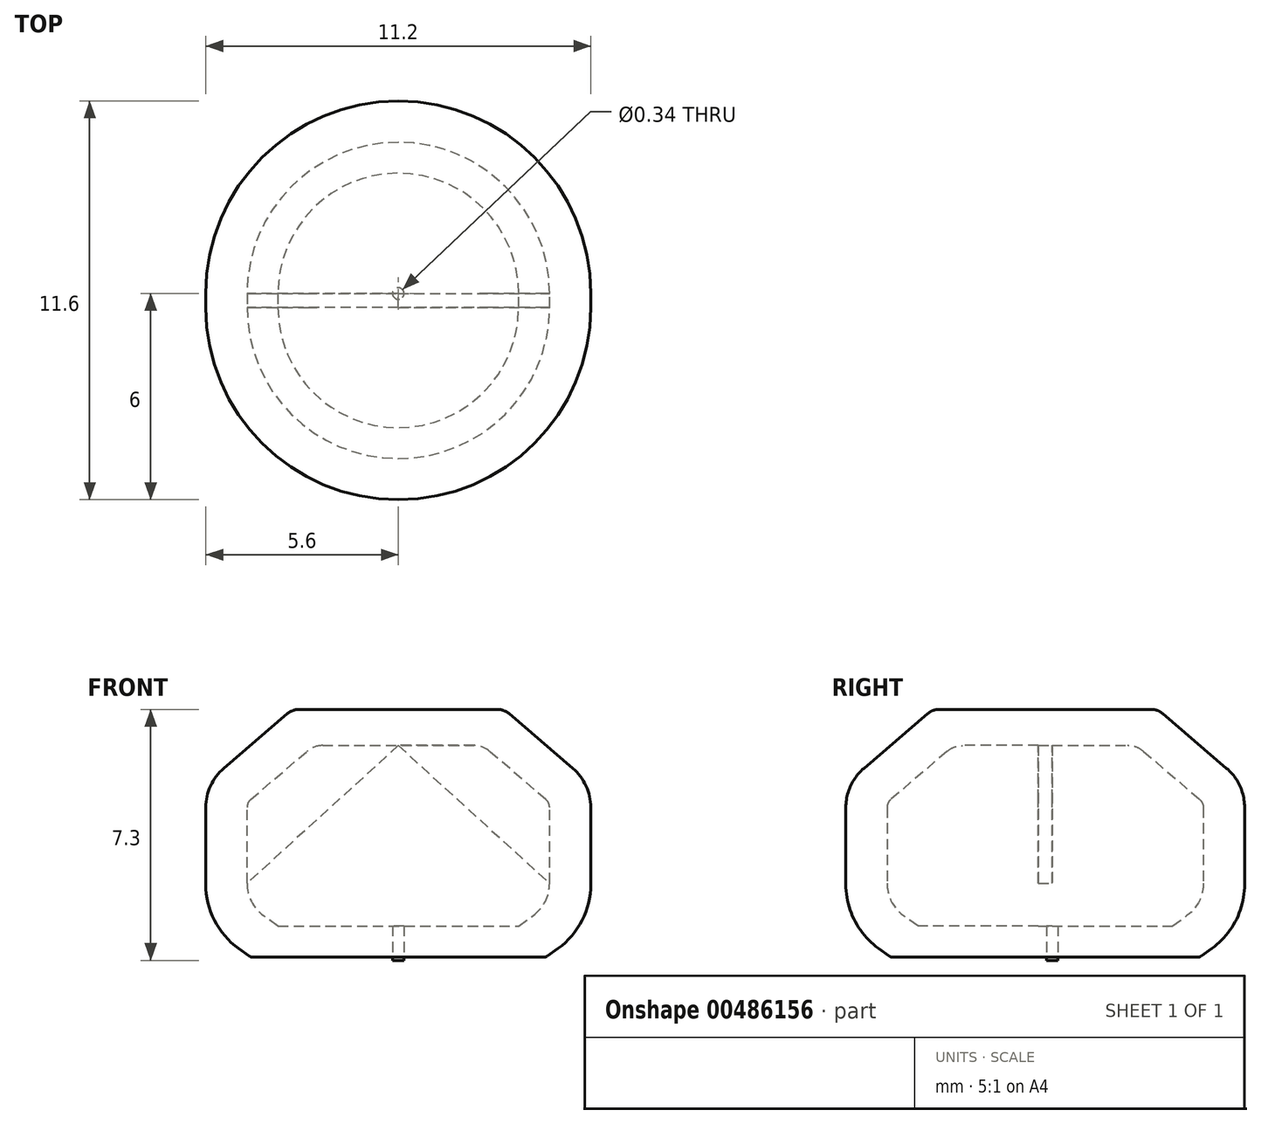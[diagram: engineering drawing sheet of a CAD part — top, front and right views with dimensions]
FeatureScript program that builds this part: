
annotation { "Feature Type Name" : "Feature", "Feature Type Description" : "" }
export const myFeature = defineFeature(function(context is Context, id is Id, definition is map)
    precondition{}
    {
        {
            assignVariable(context, id + "F0", {"name" : "l2", "anyValue" : 0.4});
        }
        {
            var Q0;
            Q0=qCreatedBy(makeId("Front.planeOp"),FACE);
            var sketch = newSketch(context, id + "F1", { "sketchPlane" : qUnion([Q0])});
            skLineSegment(sketch, "E0", {"start": v(0, 0) * mm, "end": v(4.27, 0) * mm});
            skLineSegment(sketch, "E1", {"start": v(5.6, 2.11) * mm, "end": v(5.6, 4.35) * mm});
            skLineSegment(sketch, "E2", {"start": v(2.9, 7.2) * mm, "end": v(0, 7.2) * mm});
            skLineSegment(sketch, "E3", {"start": v(4.33, 0.02) * mm, "end": v(4.65, 0.25) * mm});
            skLineSegment(sketch, "E4", {"start": v(5.08, 5.49) * mm, "end": v(3.22, 7.08) * mm});
            skLineSegment(sketch, "E5", {"start": v(0, 0) * mm, "end": v(0, 0.9) * mm});
            skLineSegment(sketch, "E6", {"start": v(0, 0.9) * mm, "end": v(3.5, 0.9) * mm});
            skLineSegment(sketch, "E7", {"start": v(4.4, 2.14) * mm, "end": v(4.4, 4.35) * mm});
            skLineSegment(sketch, "E8", {"start": v(4.3, 4.58) * mm, "end": v(2.66, 5.98) * mm});
            skLineSegment(sketch, "E9", {"start": v(2.2, 6.15) * mm, "end": v(0, 6.15) * mm});
            skLineSegment(sketch, "E10", {"start": v(0, 6.15) * mm, "end": v(0, 7.2) * mm});
            skLineSegment(sketch, "E11", {"start": v(3.5, 0.9) * mm, "end": v(3.92, 1.2) * mm});
            skPoint(sketch, "E12.visualSharp", {"position": v(5.6, 0.94) * mm});
            skArc(sketch, "E12.filletArc", {"start": v(4.65, 0.25) * mm, "mid": v(5.35, 1.06) * mm, "end": v(5.6, 2.11) * mm});
            skPoint(sketch, "E13.visualSharp", {"position": v(5.6, 5.04) * mm});
            skArc(sketch, "E13.filletArc", {"start": v(5.6, 4.35) * mm, "mid": v(5.46, 4.98) * mm, "end": v(5.08, 5.49) * mm});
            skPoint(sketch, "E14.visualSharp", {"position": v(3.08, 7.2) * mm});
            skArc(sketch, "E14.filletArc", {"start": v(3.22, 7.08) * mm, "mid": v(3.07, 7.17) * mm, "end": v(2.9, 7.2) * mm});
            skPoint(sketch, "E15.visualSharp", {"position": v(2.46, 6.15) * mm});
            skArc(sketch, "E15.filletArc", {"start": v(2.66, 5.98) * mm, "mid": v(2.45, 6.1) * mm, "end": v(2.2, 6.15) * mm});
            skPoint(sketch, "E16.visualSharp", {"position": v(4.4, 4.49) * mm});
            skArc(sketch, "E16.filletArc", {"start": v(4.4, 4.35) * mm, "mid": v(4.37, 4.48) * mm, "end": v(4.3, 4.58) * mm});
            skPoint(sketch, "E17.visualSharp", {"position": v(4.4, 1.55) * mm});
            skArc(sketch, "E17.filletArc", {"start": v(3.92, 1.2) * mm, "mid": v(4.27, 1.61) * mm, "end": v(4.4, 2.14) * mm});
            skPoint(sketch, "E18.visualSharp", {"position": v(4.3, 0) * mm});
            skArc(sketch, "E18.filletArc", {"start": v(4.27, 0) * mm, "mid": v(4.3, 0) * mm, "end": v(4.33, 0.02) * mm});
            skSolve(sketch);
        }
        {
            var Q0;
            Q0=makeQuery(id+"F1.imprint","IMPRINT",FACE,{"disambiguationData":[TD([[makeQuery(id+"F1.imprint","IMPRINT",EDGE,{"derivedFrom":sQuery(id+"F1.wireOp",EDGE,"E0")}),1.0]])]});
            extrude(context, id + "F2", {"entities" : qUnion([Q0]), "depth" : (getVariable(context, 'l2')) * mm, "offsetDistance" : 25 * mm});
        }
        {
            var Q1;
            Q1=makeQuery(id+"F2.opExtrude","SWEPT_FACE",FACE,{"disambiguationData":[OSD([sQuery(id+"F1.wireOp",EDGE,"E9")])]});
            var Q2;
            Q2=makeQuery(id+"F2.opExtrude","SWEPT_FACE",FACE,{"disambiguationData":[OSD([sQuery(id+"F1.wireOp",EDGE,"E7")])]});
            loft(context, id + "F3", {"operationType" : NewBodyOperationType.ADD, "sheetProfilesArray" : [{ "sheetProfileEntities" : qUnion([Q1]) }, { "sheetProfileEntities" : qUnion([Q2]) }]});
        }
        {
            var Q1;
            Q1=makeQuery(id+"F2.opExtrude","SWEPT_FACE",FACE,{"disambiguationData":[OSD([sQuery(id+"F1.wireOp",EDGE,"E15.filletArc")])]});
            var Q2;
            Q2=makeQuery(id+"F2.opExtrude","SWEPT_FACE",FACE,{"disambiguationData":[OSD([sQuery(id+"F1.wireOp",EDGE,"E16.filletArc")])]});
            loft(context, id + "F4", {"operationType" : NewBodyOperationType.ADD, "sheetProfilesArray" : [{ "sheetProfileEntities" : qUnion([Q1]) }, { "sheetProfileEntities" : qUnion([Q2]) }]});
        }
        {
            var Q0;
            Q0=makeQuery(id+"F1.imprint","IMPRINT",FACE,{"disambiguationData":[TD([[makeQuery(id+"F1.imprint","IMPRINT",EDGE,{"derivedFrom":sQuery(id+"F1.wireOp",EDGE,"E0")}),1.0]])]});
            var Q1;
            Q1=sQuery(id+"F1.wireOp",EDGE,"E10");
            revolve(context, id + "F5", {"operationType" : NewBodyOperationType.ADD, "entities" : qUnion([Q0]), "axis" : qUnion([Q1]), "revolveType" : RevolveType.ONE_DIRECTION, "angle" : 180 * degree, "surfaceOperationType" : NewSurfaceOperationType.NEW});
        }
        {
            var Q0;
            Q0=qCreatedBy(makeId("Front.planeOp"),FACE);
            var sketch = newSketch(context, id + "F6", { "sketchPlane" : qUnion([Q0])});
            skLineSegment(sketch, "E19", {"start": v(0, 0) * mm, "end": v(-0.4, 0) * mm});
            skLineSegment(sketch, "E20", {"start": v(-0.4, 0) * mm, "end": v(-0.4, 0.13) * mm});
            skSolve(sketch);
        }
        {
            var Q0;
            Q0=qCreatedBy(makeId("Front.planeOp"),FACE);
            cPlane(context, id + "F7", {"entities" : qUnion([Q0]), "cplaneType" : CPlaneType.OFFSET, "offset" : (getVariable(context, 'l2') / 2) * mm, "width" : 150 * mm, "height" : 150 * mm});
        }
        {
            var Q0;
            Q0=qCreatedBy(id+"F7.planeOp",FACE);
            var sketch = newSketch(context, id + "F8", { "sketchPlane" : qUnion([Q0])});
            skLineSegment(sketch, "E21", {"start": v(0, 0.03) * mm, "end": v(-0.2, 0.03) * mm});
            skLineSegment(sketch, "E22", {"start": v(-0.2, 0.03) * mm, "end": v(-0.2, 0.22) * mm});
            skLineSegment(sketch, "E23", {"start": v(0, 0.03) * mm, "end": v(0, 0.08) * mm});
            skLineSegment(sketch, "E24", {"start": v(0, 0.03) * mm, "end": v(0, 0.14) * mm});
            skPoint(sketch, "E24.endSnap0", {"position": v(0, 0.05) * mm});
            skSolve(sketch);
        }
        {
            var Q0;
            Q0=makeQuery(id+"F2.opExtrude","SWEPT_BODY",BODY,{"disambiguationData":[OSD([sQuery(id+"F1.wireOp",EDGE,"E0"),sQuery(id+"F1.wireOp",EDGE,"E1"),sQuery(id+"F1.wireOp",EDGE,"E2"),sQuery(id+"F1.wireOp",EDGE,"E3"),sQuery(id+"F1.wireOp",EDGE,"E4"),sQuery(id+"F1.wireOp",EDGE,"E5"),sQuery(id+"F1.wireOp",EDGE,"E6"),sQuery(id+"F1.wireOp",EDGE,"E7"),sQuery(id+"F1.wireOp",EDGE,"E8"),sQuery(id+"F1.wireOp",EDGE,"E9"),sQuery(id+"F1.wireOp",EDGE,"E10"),sQuery(id+"F1.wireOp",EDGE,"E11"),sQuery(id+"F1.wireOp",EDGE,"E12.filletArc"),sQuery(id+"F1.wireOp",EDGE,"E13.filletArc"),sQuery(id+"F1.wireOp",EDGE,"E14.filletArc"),sQuery(id+"F1.wireOp",EDGE,"E15.filletArc"),sQuery(id+"F1.wireOp",EDGE,"E16.filletArc"),sQuery(id+"F1.wireOp",EDGE,"E17.filletArc"),sQuery(id+"F1.wireOp",EDGE,"E18.filletArc")])]});
            var Q1;
            Q1=sQuery(id+"F8.wireOp",EDGE,"E24");
            transform(context, id + "F9", {"entities" : qUnion([Q0]), "transformType" : TransformType.ROTATION, "transformAxis" : qUnion([Q1]), "angle" : 180 * degree, "oppositeDirection" : true, "makeCopy" : true});
        }
        {
            var Q0;
            Q0=makeQuery(id+"F2.opExtrude","SWEPT_BODY",BODY,{"disambiguationData":[OSD([sQuery(id+"F1.wireOp",EDGE,"E0"),sQuery(id+"F1.wireOp",EDGE,"E1"),sQuery(id+"F1.wireOp",EDGE,"E2"),sQuery(id+"F1.wireOp",EDGE,"E3"),sQuery(id+"F1.wireOp",EDGE,"E4"),sQuery(id+"F1.wireOp",EDGE,"E5"),sQuery(id+"F1.wireOp",EDGE,"E6"),sQuery(id+"F1.wireOp",EDGE,"E7"),sQuery(id+"F1.wireOp",EDGE,"E8"),sQuery(id+"F1.wireOp",EDGE,"E9"),sQuery(id+"F1.wireOp",EDGE,"E10"),sQuery(id+"F1.wireOp",EDGE,"E11"),sQuery(id+"F1.wireOp",EDGE,"E12.filletArc"),sQuery(id+"F1.wireOp",EDGE,"E13.filletArc"),sQuery(id+"F1.wireOp",EDGE,"E14.filletArc"),sQuery(id+"F1.wireOp",EDGE,"E15.filletArc"),sQuery(id+"F1.wireOp",EDGE,"E16.filletArc"),sQuery(id+"F1.wireOp",EDGE,"E17.filletArc"),sQuery(id+"F1.wireOp",EDGE,"E18.filletArc")])]});
            var Q1;
            Q1=makeQuery(id+"F9.opPattern","COPY",BODY,{"derivedFrom":makeQuery(id+"F2.opExtrude","SWEPT_BODY",BODY,{"disambiguationData":[OSD([sQuery(id+"F1.wireOp",EDGE,"E0"),sQuery(id+"F1.wireOp",EDGE,"E1"),sQuery(id+"F1.wireOp",EDGE,"E2"),sQuery(id+"F1.wireOp",EDGE,"E3"),sQuery(id+"F1.wireOp",EDGE,"E4"),sQuery(id+"F1.wireOp",EDGE,"E5"),sQuery(id+"F1.wireOp",EDGE,"E6"),sQuery(id+"F1.wireOp",EDGE,"E7"),sQuery(id+"F1.wireOp",EDGE,"E8"),sQuery(id+"F1.wireOp",EDGE,"E9"),sQuery(id+"F1.wireOp",EDGE,"E10"),sQuery(id+"F1.wireOp",EDGE,"E11"),sQuery(id+"F1.wireOp",EDGE,"E12.filletArc"),sQuery(id+"F1.wireOp",EDGE,"E13.filletArc"),sQuery(id+"F1.wireOp",EDGE,"E14.filletArc"),sQuery(id+"F1.wireOp",EDGE,"E15.filletArc"),sQuery(id+"F1.wireOp",EDGE,"E16.filletArc"),sQuery(id+"F1.wireOp",EDGE,"E17.filletArc"),sQuery(id+"F1.wireOp",EDGE,"E18.filletArc")])]}),"instanceName":"1"});
            booleanBodies(context, id + "F10", {"operationType" : BooleanOperationType.UNION, "tools" : qUnion([Q0, Q1])});
        }
        {
            var Q0;
            {var subQ0=sQuery(id+"F1.wireOp",EDGE,"E0");var subQ1=makeQuery(id+"F5.boolean.opBoolean","MERGE",FACE,{"derivedFrom":[makeQuery(id+"F2.opExtrude","SWEPT_FACE",FACE,{"disambiguationData":[OSD([subQ0])]}),makeQuery(id+"F5.opRevolve","SWEPT_FACE",FACE,{"disambiguationData":[OSD([subQ0])]})]});var subQ2=makeQuery(id+"F10.opBoolean","MERGE",FACE,{"derivedFrom":[subQ1,makeQuery(id+"F9.opPattern","COPY",FACE,{"derivedFrom":subQ1,"instanceName":"1"})]});Q0=makeQuery(id+"FlqCVFy4lwJo1x2_1.boolean.opBoolean","MERGE",FACE,{"derivedFrom":[makeQuery(id+"F9MJncteRfP6SNt_1.opBoolean","MERGE",FACE,{"derivedFrom":[subQ2,makeQuery(id+"FLQXm9cv9NKPpU0_1.opPattern","COPY",FACE,{"derivedFrom":subQ2,"instanceName":"1"})]}),makeQuery(id+"FlqCVFy4lwJo1x2_1.opExtrude","SWEPT_FACE",FACE,{"disambiguationData":[OSD([subQ0,sQuery(id+"F1.wireOp",EDGE,"E5")])]})]});}
            var sketch = newSketch(context, id + "F11", { "sketchPlane" : qUnion([Q0])});
            skCircle(sketch, "E25", {"center": v(0, 0) * mm, "radius": 0.17 * mm});
            skSolve(sketch);
        }
        {
            var Q0;
            Q0=makeQuery(id+"F11.imprint","IMPRINT",FACE,{"disambiguationData":[TD([[makeQuery(id+"F11.imprint","IMPRINT",EDGE,{"derivedFrom":sQuery(id+"F11.wireOp",EDGE,"E25")}),-1.0]])]});
            cPlane(context, id + "F12", {"entities" : qUnion([Q0]), "cplaneType" : CPlaneType.OFFSET, "offset" : .1 * mm, "width" : 150 * mm, "height" : 150 * mm});
        }
        {
            var Q0;
            Q0=qCreatedBy(id+"F12.planeOp",FACE);
            var sketch = newSketch(context, id + "F13", { "sketchPlane" : qUnion([Q0])});
            skLineSegment(sketch, "E26", {"start": v(0, 0) * mm, "end": v(-0.33, -0.11) * mm});
            skSolve(sketch);
        }
        {
            var Q1;
            Q1=makeQuery(id+"F11.imprint","IMPRINT",FACE,{"disambiguationData":[TD([[makeQuery(id+"F11.imprint","IMPRINT",EDGE,{"derivedFrom":sQuery(id+"F11.wireOp",EDGE,"E25")}),1.0]])]});
            var Q2;
            Q2=sQuery(id+"F13.wireOp",VERTEX,"E26.start");
            loft(context, id + "F14", {"operationType" : NewBodyOperationType.ADD, "sheetProfilesArray" : [{ "sheetProfileEntities" : qUnion([Q1]) }, { "sheetProfileEntities" : qUnion([Q2]) }]});
        }
        {
            var Q0;
            Q0=makeQuery(id+"F11.imprint","IMPRINT",FACE,{"disambiguationData":[TD([[makeQuery(id+"F11.imprint","IMPRINT",EDGE,{"derivedFrom":sQuery(id+"F11.wireOp",EDGE,"E25")}),1.0]])]});
            extrude(context, id + "F15", {"entities" : qUnion([Q0]), "operationType" : NewBodyOperationType.REMOVE, "oppositeDirection" : true, "depth" : 1 * mm, "offsetDistance" : 25 * mm});
        }
        {
            var Q0;
            Q0=makeQuery(id+"F11.imprint","IMPRINT",FACE,{"disambiguationData":[TD([[makeQuery(id+"F11.imprint","IMPRINT",EDGE,{"derivedFrom":sQuery(id+"F11.wireOp",EDGE,"E25")}),1.0]])]});
            extrude(context, id + "F16", {"entities" : qUnion([Q0]), "operationType" : NewBodyOperationType.ADD, "depth" : .1 * mm, "offsetDistance" : 25 * mm});
        }
    });
